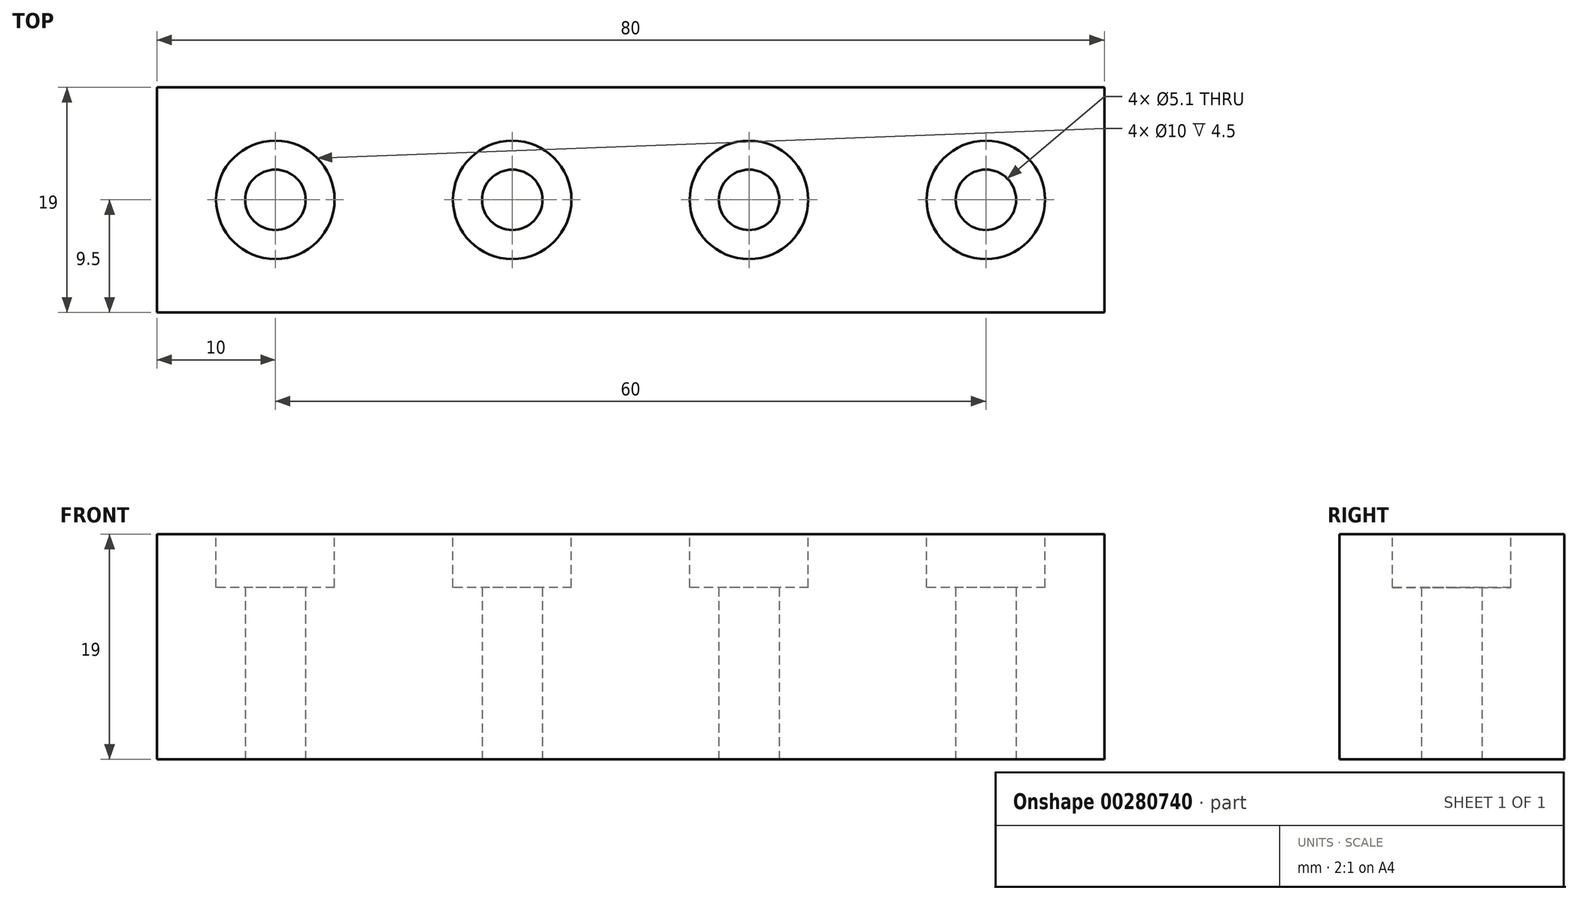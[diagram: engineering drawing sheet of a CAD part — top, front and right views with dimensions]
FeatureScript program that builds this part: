
annotation { "Feature Type Name" : "Feature", "Feature Type Description" : "" }
export const myFeature = defineFeature(function(context is Context, id is Id, definition is map)
    precondition{}
    {
        {
            var Q0;
            Q0=qCreatedBy(makeId("Top.planeOp"),FACE);
            var sketch = newSketch(context, id + "F0", { "sketchPlane" : qUnion([Q0])});
            skLineSegment(sketch, "E0.bottom", {"start": v(40, -9.5) * mm, "end": v(-40, -9.5) * mm});
            skLineSegment(sketch, "E0.top", {"start": v(40, 9.5) * mm, "end": v(-40, 9.5) * mm});
            skLineSegment(sketch, "E0.left", {"start": v(40, -9.5) * mm, "end": v(40, 9.5) * mm});
            skLineSegment(sketch, "E0.right", {"start": v(-40, -9.5) * mm, "end": v(-40, 9.5) * mm});
            skPoint(sketch, "E0.middle", {"position": v(0, 0) * mm});
            skLineSegment(sketch, "E1", {"start": v(-40, 0) * mm, "end": v(40, 0) * mm, "construction": true});
            skCircle(sketch, "E2", {"center": v(-30, 0) * mm, "radius": 2.55 * mm});
            skCircle(sketch, "E3", {"center": v(-10, 0) * mm, "radius": 2.55 * mm});
            skCircle(sketch, "E4", {"center": v(10, 0) * mm, "radius": 2.55 * mm});
            skCircle(sketch, "E5", {"center": v(30, 0) * mm, "radius": 2.55 * mm});
            skSolve(sketch);
        }
        {
            var Q0;
            Q0=makeQuery(id+"F0.imprint","IMPRINT",FACE,{"disambiguationData":[TD([[makeQuery(id+"F0.imprint","IMPRINT",EDGE,{"derivedFrom":sQuery(id+"F0.wireOp",EDGE,"E0.bottom")}),-1.0]])]});
            extrude(context, id + "F1", {"entities" : qUnion([Q0]), "depth" : 19 * mm});
        }
        {
            var Q0;
            Q0=makeQuery(id+"F1.opExtrude","CAP_FACE",FACE,{"disambiguationData":[OSD([sQuery(id+"F0.wireOp",EDGE,"E0.bottom"),sQuery(id+"F0.wireOp",EDGE,"E0.top"),sQuery(id+"F0.wireOp",EDGE,"E0.left"),sQuery(id+"F0.wireOp",EDGE,"E0.right"),sQuery(id+"F0.wireOp",EDGE,"E2"),sQuery(id+"F0.wireOp",EDGE,"E3"),sQuery(id+"F0.wireOp",EDGE,"E4"),sQuery(id+"F0.wireOp",EDGE,"E5")])],"isStart":false});
            var sketch = newSketch(context, id + "F2", { "sketchPlane" : qUnion([Q0])});
            skCircle(sketch, "E6", {"center": v(-30, 0) * mm, "radius": 5 * mm});
            skCircle(sketch, "E7", {"center": v(-10, 0) * mm, "radius": 5 * mm});
            skCircle(sketch, "E8", {"center": v(10, 0) * mm, "radius": 5 * mm});
            skCircle(sketch, "E9", {"center": v(30, 0) * mm, "radius": 5 * mm});
            skSolve(sketch);
        }
        {
            var Q0;
            Q0 = qSketchRegion(id + "F2", true);
            extrude(context, id + "F3", {"entities" : qUnion([Q0]), "operationType" : NewBodyOperationType.REMOVE, "oppositeDirection" : true, "depth" : 4.5 * mm});
        }
    });
